# Revit family: HL_Duschrinne_HL531Prblue-A-240222
name_source: partatom
category: Instalační zařizovací předměty
units: mm (PartAtom-declared; Revit-internal decimal feet)

## family parameters
Bod výpočtu místnosti = Ano
Kóta kulaté spojky = Použít průměr
Nadpis OmniClass = Deck Waste Water Drains
Ořezat dutým tvarem při načtení = Ne
Sdílené = Ano
Typ dílu = Normální
Vždy vertikální = Ano
Založené na pracovní rovině = Ne
Číslo OmniClass = 23.70.50.21.24.14

## types (1)
- HL_Duschrinne_HL531PrBlue
    AUFSATZ = 13 mm Rahmen-/Belagshöhe
    BELASTUNGSKLASSE = K3 - 300kg
    DIMENSION = DN50
    DURCHMESSER = 50 mm
    EAN = 9003076051571
    EINBAUHÖHE = 75 mm
    EINLAUFROST = Edelstahl V2A 486 x 56 mm
    GEWICHT = 2,59 [kg]
    Indexovaná poznámka = HL531PrBlue
    Komentáře k typům = Duschrinne Primus blue mit EPS-Einbauelement, Edelstahlrahmen und Abdeckung Standard
    LEISTUNG = 0,60l/s
    MATERIAL = PP/ABS/EPS-40/Edelstahl V2A
    Popis = Duschrinne
    Přípoj CW = Ne
    Přípoj HW = Ne
    Přípoj odpadních dílů = Ano
    Přípoj ventilace = Ne
    URL = https://www.hutterer-lechner.com
    VOLUMENSTROM = 0.0 L/s
    Výchozí výška = 0 mm  [stored 0 ft]
    Výrobce = HL Hutterer & Lechner GmbH

note: [stored X ft] marks values corroborated as IEEE doubles in the binary element streams (Revit-internal decimal feet)

## geometry (parser evidence)
native form markers: Sweep x10
no freeform markers — native parametric forms only
